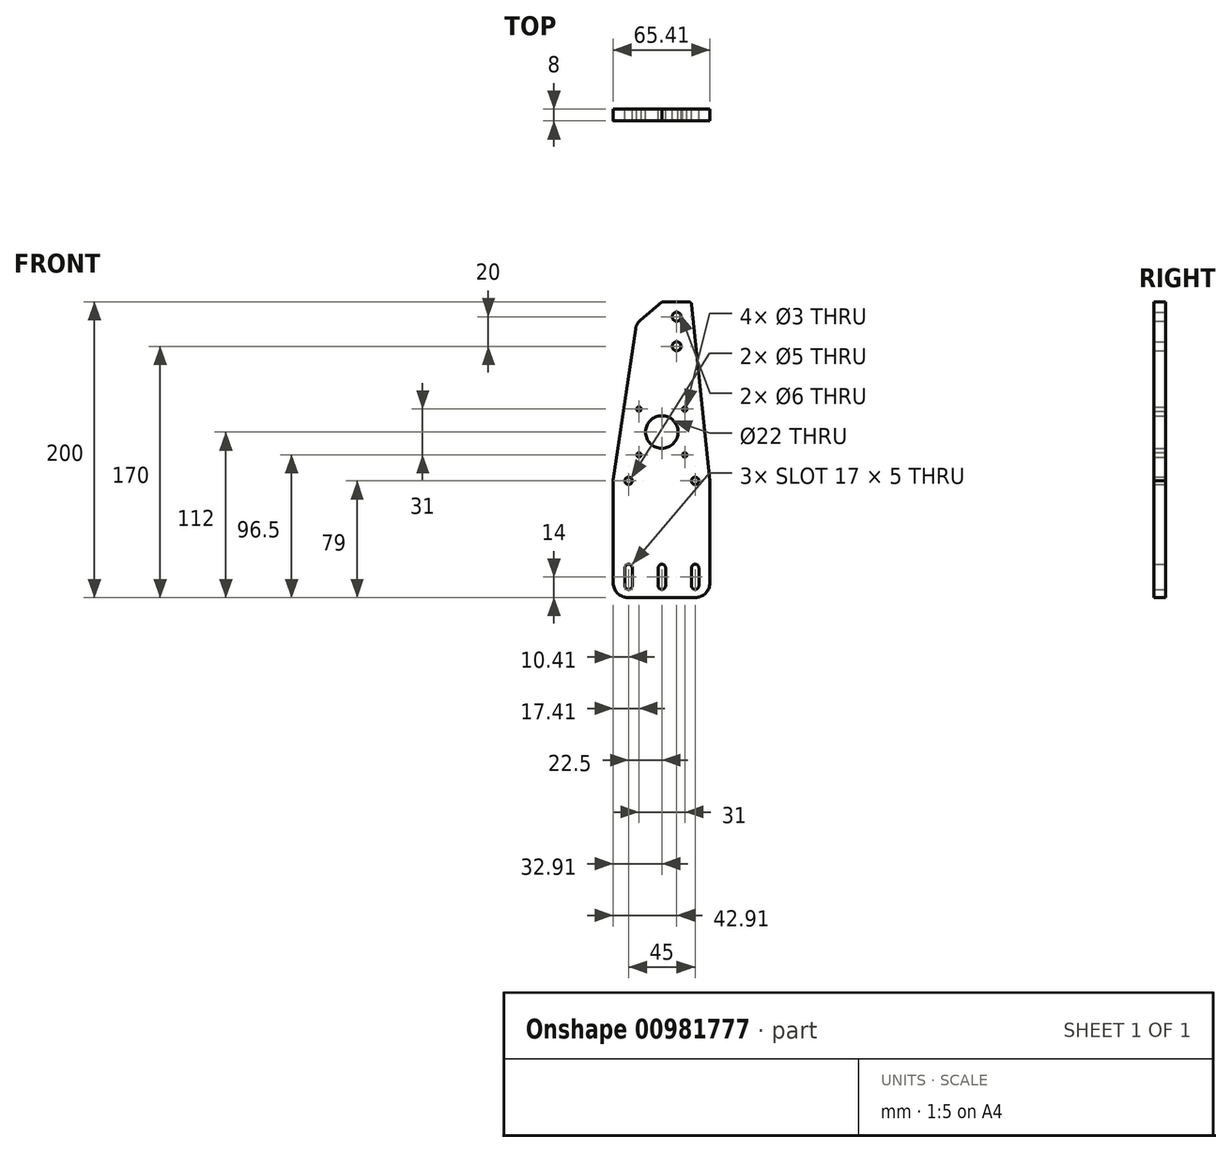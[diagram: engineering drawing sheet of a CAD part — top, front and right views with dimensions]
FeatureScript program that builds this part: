
annotation { "Feature Type Name" : "Feature", "Feature Type Description" : "" }
export const myFeature = defineFeature(function(context is Context, id is Id, definition is map)
    precondition{}
    {
        {
            var Q0;
            Q0=qCreatedBy(makeId("Front.planeOp"),FACE);
            var sketch = newSketch(context, id + "F0", { "sketchPlane" : qUnion([Q0])});
            skPoint(sketch, "E0.middle", {"position": v(0, 0) * mm});
            skCircle(sketch, "E1", {"center": v(10, 90) * mm, "radius": 3 * mm});
            skCircle(sketch, "E2", {"center": v(10, 70) * mm, "radius": 3 * mm});
            skCircle(sketch, "E3", {"center": v(0, 12) * mm, "radius": 11 * mm});
            skCircle(sketch, "E4", {"center": v(-15.5, 27.5) * mm, "radius": 1.5 * mm});
            skCircle(sketch, "E5", {"center": v(15.5, 27.5) * mm, "radius": 1.5 * mm});
            skCircle(sketch, "E6", {"center": v(15.5, -3.5) * mm, "radius": 1.5 * mm});
            skCircle(sketch, "E7", {"center": v(-15.5, -3.5) * mm, "radius": 1.5 * mm});
            skLineSegment(sketch, "E8", {"start": v(-2.5, -80) * mm, "end": v(-2.5, -92) * mm});
            skLineSegment(sketch, "E9", {"start": v(2.5, -80) * mm, "end": v(2.5, -80) * mm});
            skLineSegment(sketch, "E10", {"start": v(2.5, -80) * mm, "end": v(2.5, -92) * mm});
            skArc(sketch, "E11", {"start": v(2.5, -80) * mm, "mid": v(0, -77.5) * mm, "end": v(-2.5, -80) * mm});
            skArc(sketch, "E12", {"start": v(-2.5, -92) * mm, "mid": v(0, -94.5) * mm, "end": v(2.5, -92) * mm});
            skCircle(sketch, "E13", {"center": v(22.5, -21) * mm, "radius": 2.5 * mm});
            skCircle(sketch, "E14", {"center": v(-22.5, -21) * mm, "radius": 2.5 * mm});
            skLineSegment(sketch, "E15", {"start": v(-25, -80) * mm, "end": v(-25, -92) * mm});
            skLineSegment(sketch, "E16", {"start": v(-15.59, -74.5) * mm, "end": v(-15.59, -74.5) * mm});
            skLineSegment(sketch, "E17", {"start": v(-20, -80) * mm, "end": v(-20, -92) * mm});
            skArc(sketch, "E18", {"start": v(-20, -80) * mm, "mid": v(-22.5, -77.5) * mm, "end": v(-25, -80) * mm});
            skArc(sketch, "E19", {"start": v(-25, -92) * mm, "mid": v(-22.5, -94.5) * mm, "end": v(-20, -92) * mm});
            skLineSegment(sketch, "E20", {"start": v(20, -80) * mm, "end": v(20, -92) * mm});
            skLineSegment(sketch, "E21", {"start": v(24.48, -83.52) * mm, "end": v(24.48, -83.52) * mm});
            skLineSegment(sketch, "E22", {"start": v(25, -80) * mm, "end": v(25, -92) * mm});
            skArc(sketch, "E23", {"start": v(25, -80) * mm, "mid": v(22.5, -77.5) * mm, "end": v(20, -80) * mm});
            skArc(sketch, "E24", {"start": v(20, -92) * mm, "mid": v(22.5, -94.5) * mm, "end": v(25, -92) * mm});
            skLineSegment(sketch, "E25", {"start": v(0, 12) * mm, "end": v(0, 112.86) * mm, "construction": true});
            skLineSegment(sketch, "E26.bottom", {"start": v(18.2, 100) * mm, "end": v(0, 100) * mm});
            skLineSegment(sketch, "E26.right", {"start": v(0, 100) * mm, "end": v(0, 80) * mm});
            skLineSegment(sketch, "E27.right", {"start": v(0, 60) * mm, "end": v(0, 80) * mm});
            skLineSegment(sketch, "E28", {"start": v(0, 100) * mm, "end": v(-14.45, 87.69) * mm});
            skLineSegment(sketch, "E29", {"start": v(-32.9, -90) * mm, "end": v(-32.9, -21.73) * mm});
            skLineSegment(sketch, "E30", {"start": v(-32.8, -20.28) * mm, "end": v(-17.86, 81.53) * mm});
            skPoint(sketch, "E31.visualSharp", {"position": v(-17.31, 85.25) * mm});
            skArc(sketch, "E31.filletArc", {"start": v(-14.45, 87.69) * mm, "mid": v(-16.71, 84.92) * mm, "end": v(-17.86, 81.53) * mm});
            skPoint(sketch, "E32.visualSharp", {"position": v(-32.9, -21) * mm});
            skArc(sketch, "E32.filletArc", {"start": v(-32.8, -20.28) * mm, "mid": v(-32.88, -21) * mm, "end": v(-32.9, -21.73) * mm});
            skPoint(sketch, "E33.visualSharp", {"position": v(-32.9, -100) * mm});
            skArc(sketch, "E33.filletArc", {"start": v(-32.9, -90) * mm, "mid": v(-29.98, -97.07) * mm, "end": v(-22.9, -100) * mm});
            skLineSegment(sketch, "E34", {"start": v(0, -92) * mm, "end": v(0, -100) * mm});
            skLineSegment(sketch, "E35", {"start": v(0, -100) * mm, "end": v(22.5, -100) * mm});
            skLineSegment(sketch, "E36", {"start": v(0, -100) * mm, "end": v(-22.9, -100) * mm});
            skLineSegment(sketch, "E37", {"start": v(22.5, -100) * mm, "end": v(22.5, -100) * mm});
            skLineSegment(sketch, "E38", {"start": v(32.5, -90) * mm, "end": v(32.5, -21) * mm});
            skLineSegment(sketch, "E39", {"start": v(32.5, -21) * mm, "end": v(20.19, 98.2) * mm});
            skPoint(sketch, "E40.visualSharp", {"position": v(32.5, -100) * mm});
            skArc(sketch, "E40.filletArc", {"start": v(22.5, -100) * mm, "mid": v(29.57, -97.07) * mm, "end": v(32.5, -90) * mm});
            skPoint(sketch, "E41.visualSharp", {"position": v(20, 100) * mm});
            skArc(sketch, "E41.filletArc", {"start": v(20.19, 98.2) * mm, "mid": v(19.54, 99.49) * mm, "end": v(18.2, 100) * mm});
            skSolve(sketch);
        }
        {
            assignVariable(context, id + "F1", {"name" : "Plexiglas", "anyValue" : 8});
        }
        {
            var Q0;
            Q0=makeQuery(id+"F0.imprint","IMPRINT",FACE,{"disambiguationData":[TD([[makeQuery(id+"F0.imprint","IMPRINT",EDGE,{"derivedFrom":sQuery(id+"F0.wireOp",EDGE,"E1")}),-1.0]])]});
            extrude(context, id + "F2", {"entities" : qUnion([Q0]), "depth" : (getVariable(context, 'Plexiglas')) * mm, "offsetDistance" : 25 * mm});
        }
    });
